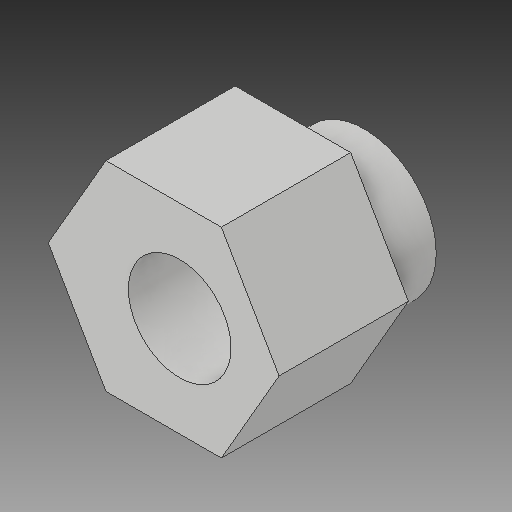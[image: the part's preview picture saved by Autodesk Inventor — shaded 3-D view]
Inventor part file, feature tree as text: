
AUTODESK INVENTOR PART (.ipt)
format: ipt  version: 2017 (Build 210142000, 142)  size: 113,152 bytes
history: native  units: mm
features: other x3, sketch x3
ambient origin geometry x8: Origin, YZ Plane, XZ Plane, XY Plane, X Axis, Y Axis, Z Axis, Center Point
bodies: Solid1 (feature_tree)
feature tree (6):
  other  "Eccentric Spacer.ipt"
  other  "Solid1::Eccentric Spacer.ipt"
  other  "TaggingFeature1"
  sketch  "Sketch1"  dims[d0=10.0mm]
  sketch  "Sketch2"
  sketch  "Sketch3"
